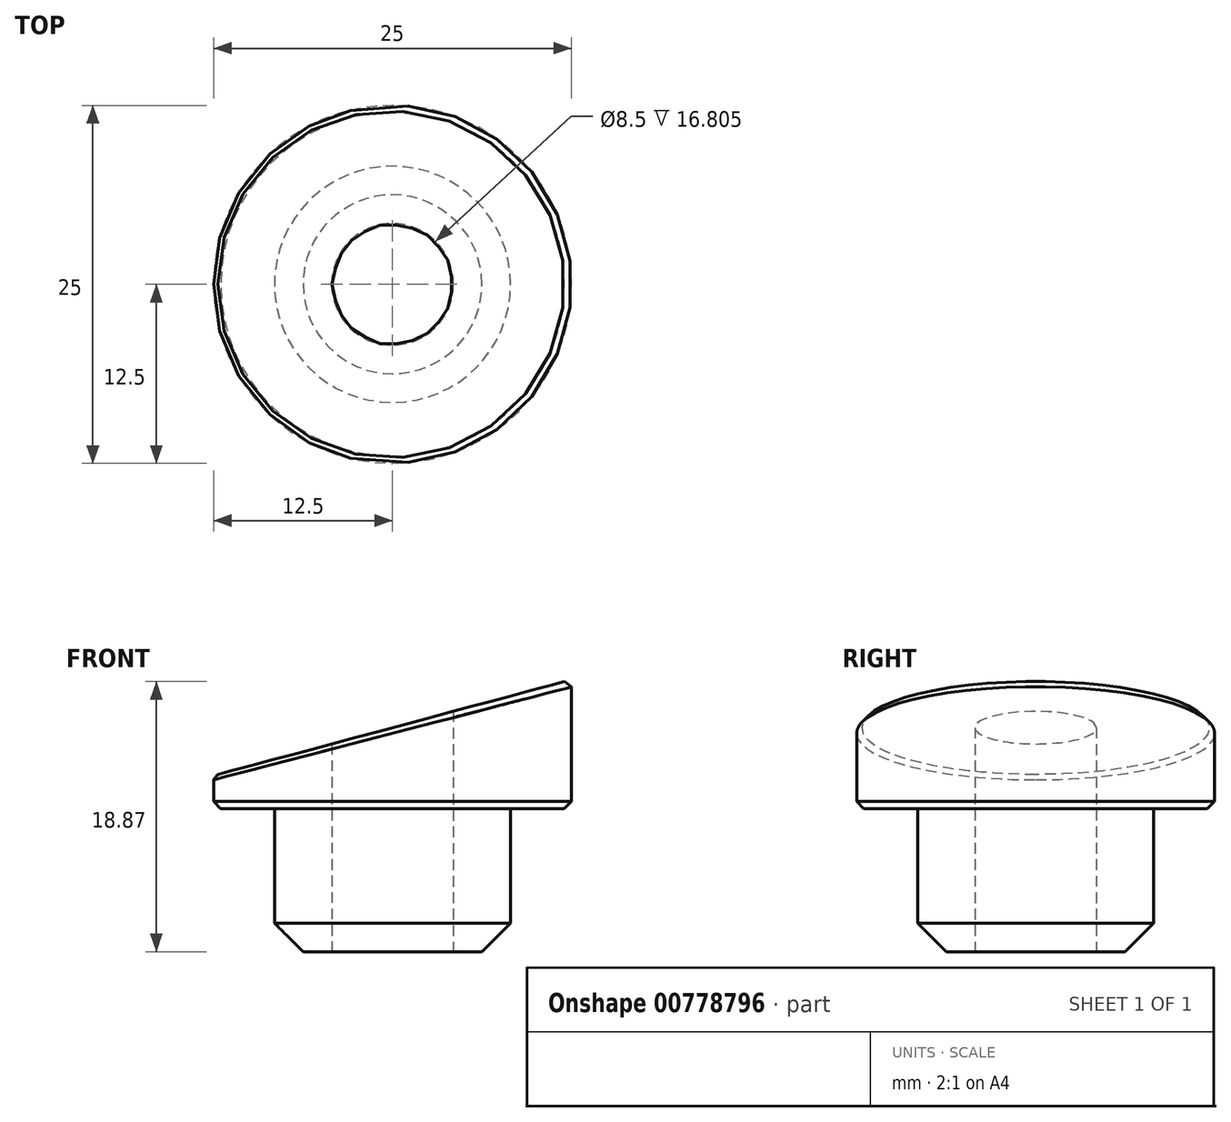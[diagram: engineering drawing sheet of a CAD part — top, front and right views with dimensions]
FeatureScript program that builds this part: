
annotation { "Feature Type Name" : "Feature", "Feature Type Description" : "" }
export const myFeature = defineFeature(function(context is Context, id is Id, definition is map)
    precondition{}
    {
        {
            var Q0;
            Q0=qCreatedBy(makeId("Top.planeOp"),FACE);
            var sketch = newSketch(context, id + "F0", { "sketchPlane" : qUnion([Q0])});
            skCircle(sketch, "E0", {"center": v(0, 0) * mm, "radius": 12.5 * mm});
            skCircle(sketch, "E1", {"center": v(0, 0) * mm, "radius": 4.25 * mm});
            skSolve(sketch);
        }
        {
            var Q0;
            Q0 = qSketchRegion(id + "F0", true);
            extrude(context, id + "F1", {"entities" : qUnion([Q0]), "depth" : 9 * mm, "offsetDistance" : 25 * mm});
        }
        {
            var Q0;
            Q0=qCreatedBy(makeId("Front.planeOp"),FACE);
            var sketch = newSketch(context, id + "F2", { "sketchPlane" : qUnion([Q0])});
            skLineSegment(sketch, "E2.0", {"start": v(-12.5, 9) * mm, "end": v(12.5, 9) * mm});
            skLineSegment(sketch, "E3", {"start": v(-12.5, 2.3) * mm, "end": v(-12.5, 10) * mm});
            skLineSegment(sketch, "E4", {"start": v(-12.5, 2.3) * mm, "end": v(12.5, 9) * mm});
            skSolve(sketch);
        }
        {
            var Q0;
            Q0 = qSketchRegion(id + "F2", true);
            extrude(context, id + "F3", {"entities" : qUnion([Q0]), "operationType" : NewBodyOperationType.REMOVE, "endBound" : BoundingType.THROUGH_ALL, "oppositeDirection" : true, "depth" : 25 * mm, "offsetDistance" : 25 * mm, "hasSecondDirection" : true, "secondDirectionBound" : BoundingType.THROUGH_ALL, "secondDirectionOppositeDirection" : false, "secondDirectionDepth" : 25 * mm});
        }
        {
            var Q0;
            Q0=makeQuery(id+"F3.boolean.opBoolean","INTERSECT",EDGE,{"derivedFrom":[makeQuery(id+"F1.opExtrude","SWEPT_FACE",FACE,{"disambiguationData":[OSD([sQuery(id+"F0.wireOp",EDGE,"E0")])]}),makeQuery(id+"F3.opExtrude","SWEPT_FACE",FACE,{"disambiguationData":[OSD([sQuery(id+"F2.wireOp",EDGE,"E4")])]})]});
            var Q1;
            Q1=makeQuery(id+"F1.opExtrude","CAP_EDGE",EDGE,{"disambiguationData":[OSD([sQuery(id+"F0.wireOp",EDGE,"E0")])],"isStart":true});
            chamfer(context, id + "F4", {"entities" : qUnion([Q0, Q1]), "width" : .5 * mm, "tangentPropagation" : true});
        }
        {
            var Q0;
            Q0=makeQuery(id+"F1.opExtrude","CAP_FACE",FACE,{"disambiguationData":[OSD([sQuery(id+"F0.wireOp",EDGE,"E0"),sQuery(id+"F0.wireOp",EDGE,"E1")])],"isStart":true});
            var sketch = newSketch(context, id + "F5", { "sketchPlane" : qUnion([Q0])});
            skCircle(sketch, "E5", {"center": v(0, 0) * mm, "radius": 8.25 * mm});
            skCircle(sketch, "E6", {"center": v(0, 0) * mm, "radius": 4.25 * mm});
            skSolve(sketch);
        }
        {
            var Q0;
            Q0 = qSketchRegion(id + "F5", true);
            extrude(context, id + "F6", {"entities" : qUnion([Q0]), "operationType" : NewBodyOperationType.ADD, "depth" : 10 * mm, "offsetDistance" : 25 * mm});
        }
        {
            var Q0;
            Q0=makeQuery(id+"F6.opExtrude","CAP_EDGE",EDGE,{"disambiguationData":[OSD([sQuery(id+"F5.wireOp",EDGE,"E5")])],"isStart":false});
            chamfer(context, id + "F7", {"entities" : qUnion([Q0]), "width" : 2 * mm, "tangentPropagation" : true});
        }
    });
